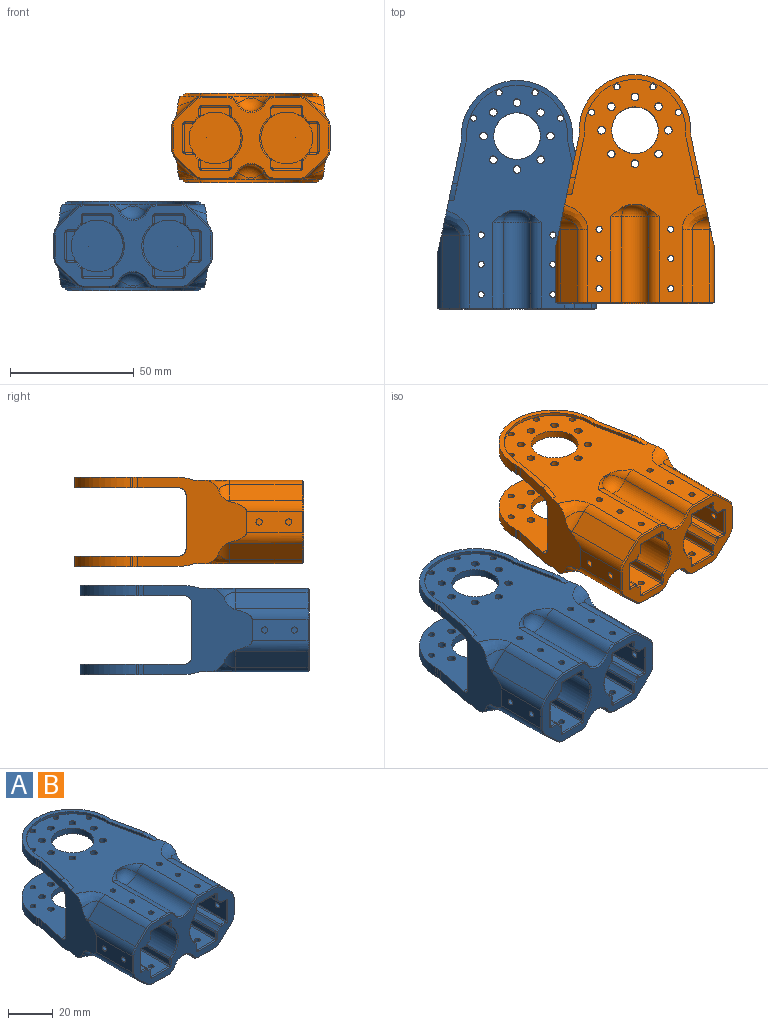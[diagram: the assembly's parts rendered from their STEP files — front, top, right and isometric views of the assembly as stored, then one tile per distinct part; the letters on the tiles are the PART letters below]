
ASSEMBLY  parts=2 mates=1
PART A: 258 faces, bbox 64.4x92.9x53.4 mm
  f0: plane 90x56.86mm, normal (0,0,1), area 2501.3mm2, adj f7,f10,f12,f13,f14,f18,f20,f22
  f1: plane 90x56.86mm, normal (0,0,-1), area 2501.3mm2, adj f7,f10,f17,f19,f21,f23,f25,f27
  f2: cylinder r=22.5mm len=45mm, axis (0,0,-1), area 296.9mm2, adj f5,f39,f41,f198
  f3: cylinder r=22.5mm len=45mm, axis (0,0,-1), area 296.9mm2, adj f4,f40,f42,f204
  f4: plane 52.4x42mm, normal (0,0,-1), area 1378mm2, adj f3,f7,f10,f18,f20,f22,f24,f26
  f5: plane 52.4x42mm, normal (0,0,1), area 1378mm2, adj f2,f7,f10,f17,f19,f21,f23,f25
  f6: plane 63x32.6mm, normal (0,-1,0), area 761mm2, adj f123,f124,f125,f126,f127,f128,f129,f130
  f7: plane 44.31x36.42mm, normal (-0.98,0.21,0), area 800.2mm2, adj f0,f1,f4,f5,f8,f16,f35,f36
  f8: plane 22.59x8.79mm, normal (-1,0,0), area 188.7mm2, adj f7,f114,f115,f119,f215,f253
  f9: plane 22.59x8.79mm, normal (1,0,0), area 188.7mm2, adj f10,f116,f117,f224,f225,f238
  f10: plane 44.31x36.42mm, normal (0.98,0.21,0), area 800.3mm2, adj f0,f1,f4,f5,f9,f16,f35,f36
  f11: cylinder r=10.5mm len=39.5mm, axis (0,-1,0), area 1183.6mm2, adj f38,f87,f91,f95,f96,f97,f98,f99
  f12: cylinder r=1.25mm len=4.3mm, axis (0,0,1), area 33.8mm2, adj f0,f84
  f13: cylinder r=1.25mm len=4.3mm, axis (0,0,1), area 33.8mm2, adj f0,f84
  f14: cylinder r=1.25mm len=4.3mm, axis (0,0,1), area 33.8mm2, adj f0,f84
  f15: cylinder r=10.5mm len=39.5mm, axis (0,-1,0), area 1183.6mm2, adj f37,f46,f50,f77,f102,f103,f104,f105
  f16: plane 53.67x21.6mm, normal (0,1,0), area 1113.2mm2, adj f7,f10,f35,f36,f172,f174,f183,f184
  f17: cylinder r=1.55mm len=3.1mm, axis (0,0,1), area 29.2mm2, adj f1,f5
  f18: cylinder r=1.55mm len=3.1mm, axis (0,0,1), area 29.2mm2, adj f0,f4
  f19: cylinder r=1.55mm len=3.1mm, axis (0,0,1), area 29.2mm2, adj f1,f5
  f20: cylinder r=1.55mm len=3.1mm, axis (0,0,1), area 29.2mm2, adj f0,f4
  f21: cylinder r=1.55mm len=3.1mm, axis (0,0,1), area 29.2mm2, adj f1,f5
  f22: cylinder r=1.55mm len=3.1mm, axis (0,0,1), area 29.2mm2, adj f0,f4
  f23: cylinder r=1.55mm len=3.1mm, axis (0,0,1), area 29.2mm2, adj f1,f5
  f24: cylinder r=1.55mm len=3.1mm, axis (0,0,1), area 29.2mm2, adj f0,f4
  f25: cylinder r=9.45mm len=18.9mm, axis (0,0,-1), area 178.1mm2, adj f1,f5
  f26: cylinder r=9.45mm len=18.9mm, axis (0,0,-1), area 178.1mm2, adj f0,f4
  f27: cylinder r=1.53mm len=3.05mm, axis (0,0,1), area 28.7mm2, adj f1,f5
  f28: cylinder r=1.53mm len=3.05mm, axis (0,0,1), area 28.7mm2, adj f0,f4
  f29: cylinder r=1.53mm len=3.05mm, axis (0,0,1), area 28.7mm2, adj f1,f5
  f30: cylinder r=1.53mm len=3.05mm, axis (0,0,1), area 28.7mm2, adj f0,f4
  f31: cylinder r=1.53mm len=3.05mm, axis (0,0,1), area 28.7mm2, adj f1,f5
  f32: cylinder r=1.53mm len=3.05mm, axis (0,0,1), area 28.7mm2, adj f0,f4
  f33: cylinder r=1.53mm len=3.05mm, axis (0,0,1), area 28.7mm2, adj f1,f5
  f34: cylinder r=1.53mm len=3.05mm, axis (0,0,1), area 28.7mm2, adj f0,f4
  f35: cylinder r=3mm len=53.67mm, axis (-1,0,0), area 249.9mm2, adj f4,f7,f10,f16
  f36: cylinder r=3mm len=53.67mm, axis (-1,0,0), area 249.9mm2, adj f5,f7,f10,f16
  f37: plane 21x21mm, normal (0,-1,0), area 346.4mm2, adj f15
  f38: plane 21x21mm, normal (0,-1,0), area 346.4mm2, adj f11
  f39: plane 4.2x0.95mm, normal (1,0,0), area 4mm2, adj f2,f5,f198,f212
  f40: plane 4.2x0.95mm, normal (1,0,0), area 4mm2, adj f3,f4,f204,f211
  f41: plane 4.2x0.95mm, normal (-1,0,0), area 4mm2, adj f2,f5,f198,f214
  f42: plane 4.2x0.95mm, normal (-1,0,0), area 4mm2, adj f3,f4,f204,f213
  f43: plane 34.5x11mm, normal (0,0,-1), area 364.8mm2, adj f46,f65,f66,f67,f82,f83,f136
  f44: plane 34.5x2.88mm, normal (-1,0,0), area 99.2mm2, adj f46,f82,f104,f140
  f45: plane 34.5x2.88mm, normal (1,0,0), area 99.2mm2, adj f46,f83,f105,f132
  f46: plane 12.78x4.17mm, normal (0,-1,0), area 31.2mm2, adj f15,f43,f44,f45,f82,f83,f104,f105
  f47: plane 34.5x11mm, normal (0,0,1), area 364.8mm2, adj f50,f68,f69,f70,f78,f79,f141
  f48: plane 34.5x2.88mm, normal (1,0,0), area 99.2mm2, adj f50,f79,f102,f137
  f49: plane 34.5x2.88mm, normal (-1,0,0), area 99.2mm2, adj f50,f78,f103,f145
  f50: plane 12.78x4.17mm, normal (0,-1,0), area 31.2mm2, adj f15,f47,f48,f49,f78,f79,f102,f103
  f51: cylinder r=6mm len=34.5mm, axis (0,-1,0), area 455mm2, adj f57,f58,f63,f250
  f52: plane 2.28x1mm, normal (0,-1,0), area 1.6mm2, adj f0,f62,f63,f64
  f53: cylinder r=6mm len=34.5mm, axis (0,-1,0), area 455mm2, adj f55,f56,f60,f241
  f54: plane 2.28x1mm, normal (0,-1,0), area 1.6mm2, adj f1,f59,f60,f61
  f55: cylinder r=5mm len=34.5mm, axis (0,-1,0), area 189.6mm2, adj f1,f53,f59,f239
  f56: cylinder r=5mm len=34.5mm, axis (0,-1,0), area 189.6mm2, adj f1,f53,f61,f243
  f57: cylinder r=5mm len=34.5mm, axis (0,-1,0), area 189.6mm2, adj f0,f51,f64,f252
  f58: cylinder r=5mm len=34.5mm, axis (0,-1,0), area 189.6mm2, adj f0,f51,f62,f248
  f59: torus R=10mm, axis (0,-1,0), area 21.7mm2, adj f1,f54,f55,f60
  f60: torus R=1mm, axis (0,-1,0), area 72.2mm2, adj f53,f54,f59,f61
  f61: torus R=10mm, axis (0,-1,0), area 21.7mm2, adj f1,f54,f56,f60
  f62: torus R=10mm, axis (0,-1,0), area 21.7mm2, adj f0,f52,f58,f63
  f63: torus R=1mm, axis (0,-1,0), area 72.2mm2, adj f51,f52,f62,f64
  f64: torus R=10mm, axis (0,-1,0), area 21.7mm2, adj f0,f52,f57,f63
  f65: cylinder r=1.25mm len=4.3mm, axis (0,0,1), area 33.8mm2, adj f0,f43
  f66: cylinder r=1.25mm len=4.3mm, axis (0,0,1), area 33.8mm2, adj f0,f43
  f67: cylinder r=1.25mm len=4.3mm, axis (0,0,1), area 33.8mm2, adj f0,f43
  f68: cylinder r=1.25mm len=4.3mm, axis (0,0,-1), area 33.8mm2, adj f1,f47
  f69: cylinder r=1.25mm len=4.3mm, axis (0,0,-1), area 33.8mm2, adj f1,f47
  f70: cylinder r=1.25mm len=4.3mm, axis (0,0,-1), area 33.8mm2, adj f1,f47
  f71: cylinder r=1.25mm len=4.3mm, axis (0,0,-1), area 33.8mm2, adj f1,f88
  f72: cylinder r=1.25mm len=4.3mm, axis (0,0,-1), area 33.8mm2, adj f1,f88
  f73: cylinder r=1.25mm len=4.3mm, axis (0,0,-1), area 33.8mm2, adj f1,f88
  f74: plane 34.5x11mm, normal (1,0,0), area 369.7mm2, adj f77,f80,f81,f114,f115,f125
  f75: plane 34.5x2.88mm, normal (0,0,-1), area 99.2mm2, adj f77,f81,f107,f124
  f76: plane 34.5x2.88mm, normal (0,0,1), area 99.2mm2, adj f77,f80,f106,f129
  f77: plane 12.78x4.17mm, normal (0,-1,0), area 31.2mm2, adj f15,f74,f75,f76,f80,f81,f106,f107
  f78: cylinder r=0.5mm len=34.5mm, axis (0,1,0), area 27.1mm2, adj f47,f49,f50,f143
  f79: cylinder r=0.5mm len=34.5mm, axis (0,1,0), area 27.1mm2, adj f47,f48,f50,f139
  f80: cylinder r=0.5mm len=34.5mm, axis (0,1,0), area 27.1mm2, adj f74,f76,f77,f127
  f81: cylinder r=0.5mm len=34.5mm, axis (0,1,0), area 27.1mm2, adj f74,f75,f77,f123
  f82: cylinder r=0.5mm len=34.5mm, axis (0,1,0), area 27.1mm2, adj f43,f44,f46,f138
  f83: cylinder r=0.5mm len=34.5mm, axis (0,1,0), area 27.1mm2, adj f43,f45,f46,f134
  f84: plane 34.5x11mm, normal (0,0,-1), area 364.8mm2, adj f12,f13,f14,f87,f112,f113,f156
  f85: plane 34.5x2.88mm, normal (-1,0,0), area 99.2mm2, adj f87,f99,f112,f160
  f86: plane 34.5x2.88mm, normal (1,0,0), area 99.2mm2, adj f87,f101,f113,f152
  f87: plane 12.78x4.17mm, normal (0,-1,0), area 31.2mm2, adj f11,f84,f85,f86,f99,f101,f112,f113
  f88: plane 34.5x11mm, normal (0,0,1), area 364.8mm2, adj f71,f72,f73,f91,f108,f109,f153
  f89: plane 34.5x2.88mm, normal (1,0,0), area 99.2mm2, adj f91,f100,f108,f149
  f90: plane 34.5x2.88mm, normal (-1,0,0), area 99.2mm2, adj f91,f96,f109,f157
  f91: plane 12.78x4.17mm, normal (0,-1,0), area 31.2mm2, adj f11,f88,f89,f90,f96,f100,f108,f109
  f92: plane 34.5x11mm, normal (-1,0,0), area 369.7mm2, adj f95,f110,f111,f116,f117,f169
  f93: plane 34.5x2.88mm, normal (0,0,1), area 99.2mm2, adj f95,f97,f110,f165
  f94: plane 34.5x2.88mm, normal (0,0,-1), area 99.2mm2, adj f95,f98,f111,f168
  f95: plane 12.78x4.17mm, normal (0,-1,0), area 31.2mm2, adj f11,f92,f93,f94,f97,f98,f110,f111
  f96: cylinder r=1mm len=34.5mm, axis (0,-1,0), area 31.6mm2, adj f11,f90,f91,f159
  f97: cylinder r=1mm len=34.5mm, axis (0,-1,0), area 31.6mm2, adj f11,f93,f95,f163
  f98: cylinder r=1mm len=34.5mm, axis (0,-1,0), area 31.6mm2, adj f11,f94,f95,f166
  f99: cylinder r=1mm len=34.5mm, axis (0,-1,0), area 31.6mm2, adj f11,f85,f87,f162
  f100: cylinder r=1mm len=34.5mm, axis (0,-1,0), area 31.6mm2, adj f11,f89,f91,f147
  f101: cylinder r=1mm len=34.5mm, axis (0,-1,0), area 31.6mm2, adj f11,f86,f87,f150
  f102: cylinder r=1mm len=34.5mm, axis (0,-1,0), area 31.6mm2, adj f15,f48,f50,f135
  f103: cylinder r=1mm len=34.5mm, axis (0,-1,0), area 31.6mm2, adj f15,f49,f50,f146
  f104: cylinder r=1mm len=34.5mm, axis (0,-1,0), area 31.6mm2, adj f15,f44,f46,f142
  f105: cylinder r=1mm len=34.5mm, axis (0,-1,0), area 31.6mm2, adj f15,f45,f46,f130
  f106: cylinder r=1mm len=34.5mm, axis (0,-1,0), area 31.6mm2, adj f15,f76,f77,f131
  f107: cylinder r=1mm len=34.5mm, axis (0,-1,0), area 31.6mm2, adj f15,f75,f77,f126
  f108: cylinder r=0.5mm len=34.5mm, axis (0,1,0), area 27.1mm2, adj f88,f89,f91,f151
  f109: cylinder r=0.5mm len=34.5mm, axis (0,1,0), area 27.1mm2, adj f88,f90,f91,f155
  f110: cylinder r=0.5mm len=34.5mm, axis (0,1,0), area 27.1mm2, adj f92,f93,f95,f167
  f111: cylinder r=0.5mm len=34.5mm, axis (0,1,0), area 27.1mm2, adj f92,f94,f95,f170
  f112: cylinder r=0.5mm len=34.5mm, axis (0,1,0), area 27.1mm2, adj f84,f85,f87,f158
  f113: cylinder r=0.5mm len=34.5mm, axis (0,1,0), area 27.1mm2, adj f84,f86,f87,f154
  f114: cylinder r=1.25mm len=5mm, axis (-1,0,0), area 39.3mm2, adj f8,f74
  f115: cylinder r=1.25mm len=5mm, axis (-1,0,0), area 39.3mm2, adj f8,f74
  f116: cylinder r=1.25mm len=5mm, axis (1,0,0), area 39.3mm2, adj f9,f92
  f117: cylinder r=1.25mm len=5mm, axis (1,0,0), area 39.3mm2, adj f9,f92
  f118: plane 29.5x6.87mm, normal (-0.68,0,0.73), area 277mm2, adj f119,f220,f222,f257
  f119: cylinder r=6mm len=29.5mm, axis (0,1,0), area 125.6mm2, adj f7,f8,f118,f221,f255
  f120: plane 29.5x6.87mm, normal (0.68,0,0.73), area 277mm2, adj f224,f228,f232,f242
  f121: plane 29.5x6.87mm, normal (-0.68,0,-0.73), area 277mm2, adj f215,f216,f218,f249
  f122: plane 29.5x6.87mm, normal (0.68,0,-0.73), area 277mm2, adj f225,f226,f230,f234
  f123: torus R=1mm, axis (0,-1,0), area 0.8mm2, adj f6,f81,f124,f125
  f124: cylinder r=0.5mm len=2.88mm, axis (1,0,0), area 2.3mm2, adj f6,f75,f123,f126
  f125: cylinder r=0.5mm len=11mm, axis (0,0,1), area 8.6mm2, adj f6,f74,f123,f127
  f126: torus R=0.5mm, axis (0,-1,0), area 0.6mm2, adj f6,f107,f124,f128
  f127: torus R=1mm, axis (0,-1,0), area 0.8mm2, adj f6,f80,f125,f129
  f128: torus R=11mm, axis (0,-1,0), area 2.2mm2, adj f6,f15,f126,f130
  f129: cylinder r=0.5mm len=2.88mm, axis (-1,0,0), area 2.3mm2, adj f6,f76,f127,f131
  f130: torus R=0.5mm, axis (0,-1,0), area 0.6mm2, adj f6,f105,f128,f132
  f131: torus R=0.5mm, axis (0,-1,0), area 0.6mm2, adj f6,f106,f129,f133
  f132: cylinder r=0.5mm len=2.88mm, axis (0,0,1), area 2.3mm2, adj f6,f45,f130,f134
  f133: torus R=11mm, axis (0,-1,0), area 2.2mm2, adj f6,f15,f131,f135
  f134: torus R=1mm, axis (0,-1,0), area 0.8mm2, adj f6,f83,f132,f136
  f135: torus R=0.5mm, axis (0,-1,0), area 0.6mm2, adj f6,f102,f133,f137
  f136: cylinder r=0.5mm len=11mm, axis (1,0,0), area 8.6mm2, adj f6,f43,f134,f138
  f137: cylinder r=0.5mm len=2.88mm, axis (0,0,1), area 2.3mm2, adj f6,f48,f135,f139
  f138: torus R=1mm, axis (0,-1,0), area 0.8mm2, adj f6,f82,f136,f140
  f139: torus R=1mm, axis (0,-1,0), area 0.8mm2, adj f6,f79,f137,f141
  f140: cylinder r=0.5mm len=2.88mm, axis (0,0,-1), area 2.3mm2, adj f6,f44,f138,f142
  f141: cylinder r=0.5mm len=11mm, axis (-1,0,0), area 8.6mm2, adj f6,f47,f139,f143
  f142: torus R=0.5mm, axis (0,-1,0), area 0.6mm2, adj f6,f104,f140,f144
  f143: torus R=1mm, axis (0,-1,0), area 0.8mm2, adj f6,f78,f141,f145
  f144: torus R=11mm, axis (0,-1,0), area 15.4mm2, adj f6,f15,f142,f146
  f145: cylinder r=0.5mm len=2.88mm, axis (0,0,-1), area 2.3mm2, adj f6,f49,f143,f146
  f146: torus R=0.5mm, axis (0,-1,0), area 0.6mm2, adj f6,f103,f144,f145
  f147: torus R=0.5mm, axis (0,-1,0), area 0.6mm2, adj f6,f100,f148,f149
  f148: torus R=11mm, axis (0,-1,0), area 15.4mm2, adj f6,f11,f147,f150
  f149: cylinder r=0.5mm len=2.88mm, axis (0,0,1), area 2.3mm2, adj f6,f89,f147,f151
  f150: torus R=0.5mm, axis (0,-1,0), area 0.6mm2, adj f6,f101,f148,f152
  f151: torus R=1mm, axis (0,-1,0), area 0.8mm2, adj f6,f108,f149,f153
  f152: cylinder r=0.5mm len=2.88mm, axis (0,0,1), area 2.3mm2, adj f6,f86,f150,f154
  f153: cylinder r=0.5mm len=11mm, axis (-1,0,0), area 8.6mm2, adj f6,f88,f151,f155
  f154: torus R=1mm, axis (0,-1,0), area 0.8mm2, adj f6,f113,f152,f156
  f155: torus R=1mm, axis (0,-1,0), area 0.8mm2, adj f6,f109,f153,f157
  f156: cylinder r=0.5mm len=11mm, axis (1,0,0), area 8.6mm2, adj f6,f84,f154,f158
  f157: cylinder r=0.5mm len=2.88mm, axis (0,0,-1), area 2.3mm2, adj f6,f90,f155,f159
  f158: torus R=1mm, axis (0,-1,0), area 0.8mm2, adj f6,f112,f156,f160
  f159: torus R=0.5mm, axis (0,-1,0), area 0.6mm2, adj f6,f96,f157,f161
  f160: cylinder r=0.5mm len=2.88mm, axis (0,0,-1), area 2.3mm2, adj f6,f85,f158,f162
  f161: torus R=11mm, axis (0,-1,0), area 2.2mm2, adj f6,f11,f159,f163
  f162: torus R=0.5mm, axis (0,-1,0), area 0.6mm2, adj f6,f99,f160,f164
  f163: torus R=0.5mm, axis (0,-1,0), area 0.6mm2, adj f6,f97,f161,f165
  f164: torus R=11mm, axis (0,-1,0), area 2.2mm2, adj f6,f11,f162,f166
  f165: cylinder r=0.5mm len=2.88mm, axis (-1,0,0), area 2.3mm2, adj f6,f93,f163,f167
  f166: torus R=0.5mm, axis (0,-1,0), area 0.6mm2, adj f6,f98,f164,f168
  f167: torus R=1mm, axis (0,-1,0), area 0.8mm2, adj f6,f110,f165,f169
  f168: cylinder r=0.5mm len=2.88mm, axis (1,0,0), area 2.3mm2, adj f6,f94,f166,f170
  f169: cylinder r=0.5mm len=11mm, axis (0,0,-1), area 8.6mm2, adj f6,f92,f167,f170
  f170: torus R=1mm, axis (0,-1,0), area 0.8mm2, adj f6,f111,f168,f169
  f171: cone r=1.25mm half-angle=59deg, axis (0,1,0), area 5.7mm2, adj f172
  f172: cylinder r=1.25mm len=6.55mm, axis (0,1,0), area 51.4mm2, adj f16,f171
  f173: cone r=1.25mm half-angle=59deg, axis (0,1,0), area 5.7mm2, adj f174
  f174: cylinder r=1.25mm len=6.55mm, axis (0,1,0), area 51.4mm2, adj f16,f173
  f175: cylinder r=1.5mm len=5.8mm, axis (0,1,0), area 54.7mm2, adj f176,f185
  f176: plane 3x3mm, normal (0,1,0), area 7.1mm2, adj f175
  f177: cylinder r=1.5mm len=5.8mm, axis (0,1,0), area 54.7mm2, adj f178,f184
  f178: plane 3x3mm, normal (0,1,0), area 7.1mm2, adj f177
  f179: cylinder r=1.5mm len=5.8mm, axis (0,1,0), area 54.7mm2, adj f180,f186
  f180: plane 3x3mm, normal (0,1,0), area 7.1mm2, adj f179
  f181: cylinder r=1.5mm len=5.8mm, axis (0,1,0), area 54.7mm2, adj f182,f183
  f182: plane 3x3mm, normal (0,1,0), area 7.1mm2, adj f181
  f183: cone r=1.5mm half-angle=45deg, axis (0,1,0), area 2.8mm2, adj f16,f181
  f184: cone r=1.5mm half-angle=45deg, axis (0,1,0), area 2.8mm2, adj f16,f177
  f185: cone r=1.5mm half-angle=45deg, axis (0,1,0), area 2.8mm2, adj f16,f175
  f186: cone r=1.5mm half-angle=45deg, axis (0,1,0), area 2.8mm2, adj f16,f179
  f187: cylinder r=1.25mm len=3mm, axis (0,0,1), area 23.6mm2, adj f0,f4
  f188: cylinder r=1.25mm len=3mm, axis (0,0,1), area 23.6mm2, adj f1,f5
  f189: cylinder r=1.25mm len=3mm, axis (0,0,1), area 23.6mm2, adj f1,f5
  f190: cylinder r=1.25mm len=3mm, axis (0,0,1), area 23.6mm2, adj f0,f4
  f191: cylinder r=1.25mm len=3mm, axis (0,0,1), area 23.6mm2, adj f0,f4
  f192: cylinder r=1.25mm len=3mm, axis (0,0,1), area 23.6mm2, adj f1,f5
  f193: cylinder r=1.25mm len=3mm, axis (0,0,1), area 23.6mm2, adj f0,f4
  f194: cylinder r=1.25mm len=3mm, axis (0,0,1), area 23.6mm2, adj f1,f5
  f195: plane 22.88x4.86mm, normal (-0.98,-0.21,0), area 25.3mm2, adj f1,f198,f200,f207
  f196: cylinder r=20.5mm len=41mm, axis (0,0,1), area 79mm2, adj f1,f198,f207,f208
  f197: plane 22.88x4.86mm, normal (0.98,-0.21,0), area 25.3mm2, adj f1,f198,f199,f208
  f198: plane 52.27x41.68mm, normal (0,0,-1), area 213.4mm2, adj f2,f7,f10,f39,f41,f195,f196,f197
  f199: cylinder r=20mm len=6.82mm, axis (-1,0,0), area 14.2mm2, adj f1,f7,f197,f198
  f200: cylinder r=20mm len=6.82mm, axis (1,0,0), area 14.2mm2, adj f1,f10,f195,f198
  f201: plane 22.88x4.86mm, normal (0.98,-0.21,0), area 25.3mm2, adj f0,f204,f205,f210
  f202: cylinder r=20.5mm len=41mm, axis (0,0,-1), area 79mm2, adj f0,f204,f209,f210
  f203: plane 22.88x4.86mm, normal (-0.98,-0.21,0), area 25.3mm2, adj f0,f204,f206,f209
  f204: plane 52.27x41.68mm, normal (0,0,1), area 213.4mm2, adj f3,f7,f10,f40,f42,f201,f202,f203
  f205: cylinder r=20mm len=6.82mm, axis (1,0,0), area 14.2mm2, adj f0,f7,f201,f204
  f206: cylinder r=20mm len=6.82mm, axis (-1,0,0), area 14.2mm2, adj f0,f10,f203,f204
  f207: cylinder r=10mm len=2.42mm, axis (0,0,1), area 2.9mm2, adj f1,f195,f196,f198
  f208: cylinder r=10mm len=2.42mm, axis (0,0,1), area 2.9mm2, adj f1,f196,f197,f198
  f209: cylinder r=10mm len=2.42mm, axis (0,0,-1), area 2.9mm2, adj f0,f202,f203,f204
  f210: cylinder r=10mm len=2.42mm, axis (0,0,-1), area 2.9mm2, adj f0,f201,f202,f204
  f211: cylinder r=10mm len=4.2mm, axis (0,0,1), area 8.8mm2, adj f4,f10,f40,f204
  f212: cylinder r=10mm len=4.2mm, axis (0,0,1), area 8.8mm2, adj f5,f10,f39,f198
  f213: cylinder r=10mm len=4.2mm, axis (0,0,1), area 8.8mm2, adj f4,f7,f42,f204
  f214: cylinder r=10mm len=4.2mm, axis (0,0,1), area 8.8mm2, adj f5,f7,f41,f198
  f215: cylinder r=6mm len=29.5mm, axis (0,-1,0), area 125.6mm2, adj f7,f8,f121,f217,f251
  f216: cylinder r=5mm len=8.67mm, axis (0.73,0,-0.68), area 32.8mm2, adj f7,f121,f217,f219
  f217: torus R=11mm, axis (0,1,0), area 0.5mm2, adj f7,f215,f216
  f218: cylinder r=6mm len=29.5mm, axis (0,1,0), area 132.9mm2, adj f1,f121,f219,f247
  f219: bspline ~12x10.35mm, area 63.4mm2, adj f1,f7,f216,f218
  f220: cylinder r=5mm len=8.67mm, axis (-0.73,0,-0.68), area 32.8mm2, adj f7,f118,f221,f223
  f221: torus R=11mm, axis (0,1,0), area 0.5mm2, adj f7,f119,f220
  f222: cylinder r=6mm len=29.5mm, axis (0,1,0), area 132.9mm2, adj f0,f118,f223,f256
  f223: bspline ~12.26x12mm, area 63.4mm2, adj f0,f7,f220,f222
  f224: cylinder r=6mm len=29.5mm, axis (0,1,0), area 125.6mm2, adj f9,f10,f120,f229,f240
  f225: cylinder r=6mm len=29.5mm, axis (0,-1,0), area 125.6mm2, adj f9,f10,f122,f227,f236
  f226: cylinder r=5mm len=8.67mm, axis (0.73,0,0.68), area 32.8mm2, adj f10,f122,f227,f231
  f227: torus R=11mm, axis (0,1,0), area 0.5mm2, adj f10,f225,f226
  f228: cylinder r=5mm len=8.67mm, axis (-0.73,0,0.68), area 32.8mm2, adj f10,f120,f229,f233
  f229: torus R=11mm, axis (0,1,0), area 0.5mm2, adj f10,f224,f228
  f230: cylinder r=6mm len=29.5mm, axis (0,-1,0), area 132.9mm2, adj f1,f122,f231,f235
  f231: bspline ~12x10.83mm, area 63.4mm2, adj f1,f10,f226,f230
  f232: cylinder r=6mm len=29.5mm, axis (0,-1,0), area 132.9mm2, adj f0,f120,f233,f244
  f233: bspline ~12x10.35mm, area 63.4mm2, adj f0,f10,f228,f232
  f234: plane 7.21x6.77mm, normal (0.48,-0.71,-0.52), area 6.6mm2, adj f6,f122,f235,f236
  f235: cone r=5.5mm half-angle=45deg, axis (0,1,0), area 3.1mm2, adj f6,f230,f234,f237
  f236: cone r=5.5mm half-angle=45deg, axis (0,1,0), area 3.3mm2, adj f6,f225,f234,f238
  f237: plane 9.34x0.5mm, normal (0,-0.71,-0.71), area 6.6mm2, adj f1,f6,f235,f239
  f238: plane 8.79x0.5mm, normal (0.71,-0.71,0), area 6.2mm2, adj f6,f9,f236,f240
  f239: cone r=4.5mm half-angle=45deg, axis (0,1,0), area 3.7mm2, adj f6,f55,f237,f241
  f240: cone r=5.5mm half-angle=45deg, axis (0,1,0), area 3.3mm2, adj f6,f224,f238,f242
  f241: cone r=6.5mm half-angle=45deg, axis (0,-1,0), area 9.7mm2, adj f6,f53,f239,f243
  f242: plane 7.21x6.77mm, normal (0.48,-0.71,0.52), area 6.6mm2, adj f6,f120,f240,f244
  f243: cone r=4.5mm half-angle=45deg, axis (0,1,0), area 3.7mm2, adj f6,f56,f241,f245
  f244: cone r=5.5mm half-angle=45deg, axis (0,1,0), area 3.1mm2, adj f6,f232,f242,f246
  f245: plane 9.34x0.5mm, normal (0,-0.71,-0.71), area 6.6mm2, adj f1,f6,f243,f247
  f246: plane 9.34x0.5mm, normal (0,-0.71,0.71), area 6.6mm2, adj f0,f6,f244,f248
  f247: cone r=5.5mm half-angle=45deg, axis (0,1,0), area 3.1mm2, adj f6,f218,f245,f249
  f248: cone r=4.5mm half-angle=45deg, axis (0,1,0), area 3.7mm2, adj f6,f58,f246,f250
  f249: plane 7.21x6.77mm, normal (-0.48,-0.71,-0.52), area 6.6mm2, adj f6,f121,f247,f251
  f250: cone r=6mm half-angle=45deg, axis (0,-1,0), area 9.7mm2, adj f6,f51,f248,f252
  f251: cone r=5.5mm half-angle=45deg, axis (0,1,0), area 3.3mm2, adj f6,f215,f249,f253
  f252: cone r=4.5mm half-angle=45deg, axis (0,1,0), area 3.7mm2, adj f6,f57,f250,f254
  f253: plane 8.79x0.5mm, normal (-0.71,-0.71,0), area 6.2mm2, adj f6,f8,f251,f255
  f254: plane 9.34x0.5mm, normal (0,-0.71,0.71), area 6.6mm2, adj f0,f6,f252,f256
  f255: cone r=5.5mm half-angle=45deg, axis (0,1,0), area 3.3mm2, adj f6,f119,f253,f257
  f256: cone r=5.5mm half-angle=45deg, axis (0,1,0), area 3.1mm2, adj f6,f222,f254,f257
  f257: plane 7.21x6.77mm, normal (-0.48,-0.71,0.52), area 6.6mm2, adj f6,f118,f255,f256
PART B: same geometry as A
PLACE A t=(-63.16,24.18,-26.04)mm
PLACE B t=(-15.5,26.46,17.62)mm
MATE parallel A.f2 <-> B.f2  axis (0,0,1) through (-63.16,24.18,7.56)mm
